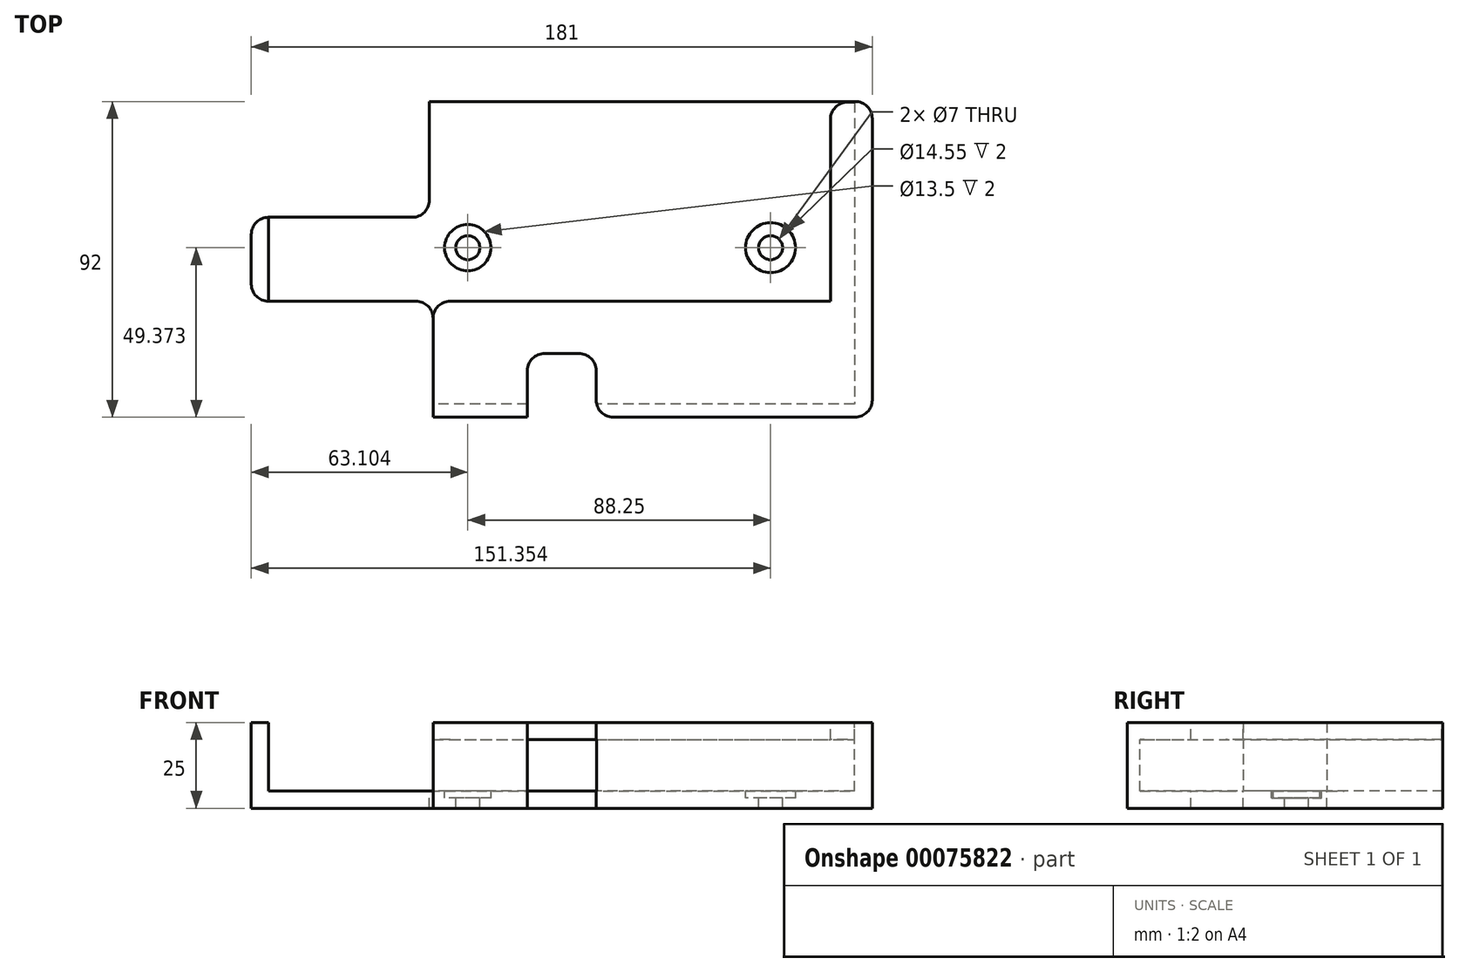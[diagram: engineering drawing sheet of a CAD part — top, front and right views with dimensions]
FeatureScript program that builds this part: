
annotation { "Feature Type Name" : "Feature", "Feature Type Description" : "" }
export const myFeature = defineFeature(function(context is Context, id is Id, definition is map)
    precondition{}
    {
        {
            var Q0;
            Q0=qCreatedBy(makeId("Top.planeOp"),FACE);
            var sketch = newSketch(context, id + "F0", { "sketchPlane" : qUnion([Q0])});
            skLineSegment(sketch, "E0.bottom", {"start": v(-90.5, 55.49) * mm, "end": v(90.5, 55.49) * mm});
            skLineSegment(sketch, "E0.top", {"start": v(-90.5, -36.51) * mm, "end": v(90.5, -36.51) * mm});
            skLineSegment(sketch, "E0.left", {"start": v(-90.5, 55.49) * mm, "end": v(-90.5, -36.51) * mm});
            skLineSegment(sketch, "E0.right", {"start": v(90.5, 55.49) * mm, "end": v(90.5, -36.51) * mm});
            skLineSegment(sketch, "E1.bottom", {"start": v(-25, 55.49) * mm, "end": v(25, 55.49) * mm});
            skSolve(sketch);
        }
        {
            var Q0;
            {var subQ5=sQuery(id+"F0.wireOp",EDGE,"E0.right");Q0=makeQuery(id+"F0.imprint","IMPRINT",FACE,{"disambiguationData":[TD([[makeQuery(id+"F0.imprint","IMPRINT",EDGE,{"derivedFrom":subQ5}),-1.0]])]});}
            var Q1;
            {var subQ7=sQuery(id+"F0.wireOp",EDGE,"E0.left");Q1=makeQuery(id+"F0.imprint","IMPRINT",FACE,{"disambiguationData":[TD([[makeQuery(id+"F0.imprint","IMPRINT",EDGE,{"derivedFrom":subQ7}),1.0]])]});}
            var Q2;
            {var subQ0=sQuery(id+"F0.wireOp",EDGE,"E1.right");Q2=makeQuery(id+"F0.imprint","IMPRINT",FACE,{"disambiguationData":[TD([[makeQuery(id+"F0.imprint","IMPRINT",EDGE,{"derivedFrom":subQ0}),1.0]])]});}
            var Q3;
            {var subQ0=sQuery(id+"F0.wireOp",EDGE,"E1.left");Q3=makeQuery(id+"F0.imprint","IMPRINT",FACE,{"disambiguationData":[TD([[makeQuery(id+"F0.imprint","IMPRINT",EDGE,{"derivedFrom":subQ0}),-1.0]])]});}
            extrude(context, id + "F1", {"entities" : qUnion([Q0, Q1, Q2, Q3]), "depth" : 25 * mm});
        }
        {
            var Q0;
            Q0=makeQuery(id+"F1.opExtrude","CAP_FACE",FACE,{"disambiguationData":[OSD([sQuery(id+"F0.wireOp",EDGE,"E0.bottom"),sQuery(id+"F0.wireOp",EDGE,"E0.top"),sQuery(id+"F0.wireOp",EDGE,"E0.left"),sQuery(id+"F0.wireOp",EDGE,"E0.right"),sQuery(id+"F0.wireOp",EDGE,"E1.top"),sQuery(id+"F0.wireOp",EDGE,"E1.left"),sQuery(id+"F0.wireOp",EDGE,"E1.right")])],"isStart":false});
            var sketch = newSketch(context, id + "F2", { "sketchPlane" : qUnion([Q0])});
            skLineSegment(sketch, "E2.bottom", {"start": v(-85, 55.49) * mm, "end": v(85, 55.49) * mm});
            skLineSegment(sketch, "E2.top", {"start": v(-85, -30.32) * mm, "end": v(85, -30.32) * mm});
            skLineSegment(sketch, "E2.left", {"start": v(-85, 55.49) * mm, "end": v(-85, -30.32) * mm});
            skLineSegment(sketch, "E2.right", {"start": v(85, 55.49) * mm, "end": v(85, -30.32) * mm});
            skLineSegment(sketch, "E3", {"start": v(0, 55.49) * mm, "end": v(0, 0) * mm});
            skPoint(sketch, "E3.startSnap0", {"position": v(0, 55.49) * mm});
            skLineSegment(sketch, "E4", {"start": v(0, 0) * mm, "end": v(0, -30.32) * mm});
            skLineSegment(sketch, "E5", {"start": v(-85, 0) * mm, "end": v(0, 0) * mm});
            skLineSegment(sketch, "E6", {"start": v(85, 0) * mm, "end": v(0, 0) * mm});
            skSolve(sketch);
        }
        {
            var Q0;
            Q0=makeQuery(id+"F2.imprint","IMPRINT",FACE,{"disambiguationData":[TD([[makeQuery(id+"F2.imprint","IMPRINT",EDGE,{"derivedFrom":makeQuery(id+"F1.opExtrude","CAP_EDGE",EDGE,{"disambiguationData":[OSD([sQuery(id+"F0.wireOp",EDGE,"E0.top")])],"isStart":false})}),1.0]])]});
            var sketch = newSketch(context, id + "F3", { "sketchPlane" : qUnion([Q0])});
            skPoint(sketch, "E7", {"position": v(0, -17.95) * mm});
            skLineSegment(sketch, "E8", {"start": v(0, -17.95) * mm, "end": v(10, -17.95) * mm});
            skLineSegment(sketch, "E9", {"start": v(10, -17.95) * mm, "end": v(10, -36.51) * mm});
            skLineSegment(sketch, "E10", {"start": v(0, -17.95) * mm, "end": v(-10, -17.95) * mm});
            skLineSegment(sketch, "E11", {"start": v(-10, -17.95) * mm, "end": v(-10, -36.51) * mm});
            skSolve(sketch);
        }
        {
            var Q0;
            {var subQ7=makeQuery(id+"F2.imprint","IMPRINT",EDGE,{"derivedFrom":makeQuery(id+"F1.opExtrude","CAP_EDGE",EDGE,{"disambiguationData":[OSD([sQuery(id+"F0.wireOp",EDGE,"E0.top")])],"isStart":false})});var subQ9=sQuery(id+"F3.wireOp",EDGE,"E9");var subQ11=makeQuery(id+"F3.imprint","INTERSECT",VERTEX,{"derivedFrom":[subQ7,subQ9]});Q0=makeQuery(id+"F3.imprint","IMPRINT",FACE,{"disambiguationData":[TD([[makeQuery(id+"F3.imprint","IMPRINT",EDGE,{"disambiguationData":[TD([[subQ11,1.0]])],"derivedFrom":subQ7}),1.0]])]});}
            var Q1;
            {var subQ2=sQuery(id+"F3.wireOp",EDGE,"E8");Q1=makeQuery(id+"F3.imprint","IMPRINT",FACE,{"disambiguationData":[TD([[makeQuery(id+"F3.imprint","IMPRINT",EDGE,{"derivedFrom":subQ2}),-1.0]])]});}
            extrude(context, id + "F4", {"entities" : qUnion([Q0, Q1]), "operationType" : NewBodyOperationType.REMOVE, "oppositeDirection" : true, "depth" : 25 * mm});
        }
        {
            var Q0;
            Q0=makeQuery(id+"F1.opExtrude","CAP_FACE",FACE,{"disambiguationData":[OSD([sQuery(id+"F0.wireOp",EDGE,"E0.bottom"),sQuery(id+"F0.wireOp",EDGE,"E0.top"),sQuery(id+"F0.wireOp",EDGE,"E0.left"),sQuery(id+"F0.wireOp",EDGE,"E0.right"),sQuery(id+"F0.wireOp",EDGE,"E1.top"),sQuery(id+"F0.wireOp",EDGE,"E1.left"),sQuery(id+"F0.wireOp",EDGE,"E1.right")])],"isStart":false});
            var sketch = newSketch(context, id + "F5", { "sketchPlane" : qUnion([Q0])});
            skLineSegment(sketch, "E12", {"start": v(83.31, 55.49) * mm, "end": v(83.31, -2.74) * mm});
            skLineSegment(sketch, "E13", {"start": v(83.31, -2.74) * mm, "end": v(-37.52, -2.74) * mm});
            skLineSegment(sketch, "E14", {"start": v(-37.52, -2.74) * mm, "end": v(-37.52, -36.51) * mm});
            skSolve(sketch);
        }
        {
            var Q0;
            {var subQ7=sQuery(id+"F5.wireOp",EDGE,"E12");Q0=makeQuery(id+"F5.imprint","IMPRINT",FACE,{"disambiguationData":[TD([[makeQuery(id+"F5.imprint","IMPRINT",EDGE,{"derivedFrom":subQ7}),-1.0]])]});}
            extrude(context, id + "F6", {"entities" : qUnion([Q0]), "operationType" : NewBodyOperationType.REMOVE, "oppositeDirection" : true, "depth" : 20 * mm});
        }
        {
            var Q0;
            Q0=makeQuery(id+"F6.boolean.opBoolean","COPY",FACE,{"derivedFrom":makeQuery(id+"F6.opExtrude","CAP_FACE",FACE,{"disambiguationData":[OSD([sQuery(id+"F0.wireOp",EDGE,"E0.bottom"),sQuery(id+"F0.wireOp",EDGE,"E0.top"),sQuery(id+"F0.wireOp",EDGE,"E0.left"),sQuery(id+"F0.wireOp",EDGE,"E1.top"),sQuery(id+"F0.wireOp",EDGE,"E1.left"),sQuery(id+"F0.wireOp",EDGE,"E1.right"),sQuery(id+"F5.wireOp",EDGE,"E12"),sQuery(id+"F5.wireOp",EDGE,"E13"),sQuery(id+"F5.wireOp",EDGE,"E14")])],"isStart":false})});
            var sketch = newSketch(context, id + "F7", { "sketchPlane" : qUnion([Q0])});
            skLineSegment(sketch, "E15.bottom", {"start": v(-37.52, -2.74) * mm, "end": v(-90.5, -2.74) * mm});
            skLineSegment(sketch, "E15.top", {"start": v(-37.52, -36.51) * mm, "end": v(-90.5, -36.51) * mm});
            skLineSegment(sketch, "E15.left", {"start": v(-37.52, -2.74) * mm, "end": v(-37.52, -36.51) * mm});
            skLineSegment(sketch, "E15.right", {"start": v(-90.5, -2.74) * mm, "end": v(-90.5, -36.51) * mm});
            skLineSegment(sketch, "E16.bottom", {"start": v(-90.5, 55.49) * mm, "end": v(-38.59, 55.49) * mm});
            skLineSegment(sketch, "E16.top", {"start": v(-90.5, 21.71) * mm, "end": v(-38.59, 21.71) * mm});
            skLineSegment(sketch, "E16.left", {"start": v(-90.5, 55.49) * mm, "end": v(-90.5, 21.71) * mm});
            skLineSegment(sketch, "E16.right", {"start": v(-38.59, 55.49) * mm, "end": v(-38.59, 21.71) * mm});
            skSolve(sketch);
        }
        {
            var Q0;
            Q0=makeQuery(id+"F7.imprint","IMPRINT",FACE,{"disambiguationData":[TD([[makeQuery(id+"F7.imprint","IMPRINT",EDGE,{"derivedFrom":sQuery(id+"F7.wireOp",EDGE,"E16.bottom")}),-1.0]])]});
            var Q1;
            Q1=makeQuery(id+"F7.imprint","IMPRINT",FACE,{"disambiguationData":[TD([[makeQuery(id+"F7.imprint","IMPRINT",EDGE,{"derivedFrom":sQuery(id+"F7.wireOp",EDGE,"E15.bottom")}),1.0]])]});
            extrude(context, id + "F8", {"entities" : qUnion([Q0, Q1]), "operationType" : NewBodyOperationType.REMOVE, "oppositeDirection" : true, "depth" : 25 * mm});
        }
        {
            var Q0;
            Q0=makeQuery(id+"F6.boolean.opBoolean","COPY",FACE,{"derivedFrom":makeQuery(id+"F6.opExtrude","CAP_FACE",FACE,{"disambiguationData":[OSD([sQuery(id+"F0.wireOp",EDGE,"E0.bottom"),sQuery(id+"F0.wireOp",EDGE,"E0.top"),sQuery(id+"F0.wireOp",EDGE,"E0.left"),sQuery(id+"F0.wireOp",EDGE,"E1.top"),sQuery(id+"F0.wireOp",EDGE,"E1.left"),sQuery(id+"F0.wireOp",EDGE,"E1.right"),sQuery(id+"F5.wireOp",EDGE,"E12"),sQuery(id+"F5.wireOp",EDGE,"E13"),sQuery(id+"F5.wireOp",EDGE,"E14")])],"isStart":false})});
            var sketch = newSketch(context, id + "F9", { "sketchPlane" : qUnion([Q0])});
            skLineSegment(sketch, "E17", {"start": v(-90.5, 21.71) * mm, "end": v(-85.5, 21.71) * mm});
            skLineSegment(sketch, "E18", {"start": v(-85.5, 21.71) * mm, "end": v(-85.5, -2.74) * mm});
            skSolve(sketch);
        }
        {
            var Q0;
            Q0=makeQuery(id+"F9.imprint","IMPRINT",FACE,{"disambiguationData":[TD([[makeQuery(id+"F9.imprint","IMPRINT",EDGE,{"derivedFrom":sQuery(id+"F9.wireOp",EDGE,"E17")}),-1.0]])]});
            extrude(context, id + "F10", {"entities" : qUnion([Q0]), "operationType" : NewBodyOperationType.ADD, "depth" : 20 * mm});
        }
        {
            var Q0;
            Q0=makeQuery(id+"F6.boolean.opBoolean","COPY",FACE,{"derivedFrom":makeQuery(id+"F6.opExtrude","SWEPT_FACE",FACE,{"disambiguationData":[OSD([sQuery(id+"F5.wireOp",EDGE,"E13")])]})});
            var sketch = newSketch(context, id + "F11", { "sketchPlane" : qUnion([Q0])});
            skLineSegment(sketch, "E19.bottom", {"start": v(37.52, 5) * mm, "end": v(-83.31, 5) * mm});
            skLineSegment(sketch, "E19.top", {"start": v(37.52, 20) * mm, "end": v(-83.31, 20) * mm});
            skLineSegment(sketch, "E19.left", {"start": v(37.52, 5) * mm, "end": v(37.52, 20) * mm});
            skLineSegment(sketch, "E19.right", {"start": v(-83.31, 5) * mm, "end": v(-83.31, 20) * mm});
            skLineSegment(sketch, "E20", {"start": v(37.52, 20) * mm, "end": v(37.52, 25) * mm});
            skSolve(sketch);
        }
        {
            var Q0;
            Q0=makeQuery(id+"F11.imprint","IMPRINT",FACE,{"disambiguationData":[TD([[makeQuery(id+"F11.imprint","IMPRINT",EDGE,{"derivedFrom":sQuery(id+"F11.wireOp",EDGE,"E19.bottom")}),1.0]])]});
            extrude(context, id + "F12", {"entities" : qUnion([Q0]), "operationType" : NewBodyOperationType.REMOVE, "oppositeDirection" : true, "depth" : 30 * mm});
        }
        {
            var Q0;
            Q0=makeQuery(id+"F12.boolean.opBoolean","MERGE",FACE,{"derivedFrom":[makeQuery(id+"F6.boolean.opBoolean","COPY",FACE,{"derivedFrom":makeQuery(id+"F6.opExtrude","CAP_FACE",FACE,{"disambiguationData":[OSD([sQuery(id+"F0.wireOp",EDGE,"E0.bottom"),sQuery(id+"F0.wireOp",EDGE,"E0.top"),sQuery(id+"F0.wireOp",EDGE,"E0.left"),sQuery(id+"F0.wireOp",EDGE,"E1.top"),sQuery(id+"F0.wireOp",EDGE,"E1.left"),sQuery(id+"F0.wireOp",EDGE,"E1.right"),sQuery(id+"F5.wireOp",EDGE,"E12"),sQuery(id+"F5.wireOp",EDGE,"E13"),sQuery(id+"F5.wireOp",EDGE,"E14")])],"isStart":false})}),makeQuery(id+"F12.opExtrude","SWEPT_FACE",FACE,{"disambiguationData":[OSD([sQuery(id+"F11.wireOp",EDGE,"E19.bottom")])]})]});
            var sketch = newSketch(context, id + "F13", { "sketchPlane" : qUnion([Q0])});
            skLineSegment(sketch, "E21", {"start": v(-85.5, 12.86) * mm, "end": v(-27.4, 12.86) * mm});
            skLineSegment(sketch, "E22", {"start": v(-27.4, 12.86) * mm, "end": v(60.85, 12.86) * mm});
            skLineSegment(sketch, "E23", {"start": v(60.85, 12.86) * mm, "end": v(83.31, 12.86) * mm});
            skCircle(sketch, "E24", {"center": v(-27.4, 12.86) * mm, "radius": 3.5 * mm});
            skCircle(sketch, "E25", {"center": v(60.85, 12.86) * mm, "radius": 3.5 * mm});
            skSolve(sketch);
        }
        {
            var Q0;
            {var subQ0=sQuery(id+"F13.wireOp",EDGE,"E23");var subQ1=sQuery(id+"F13.wireOp",EDGE,"E22");var subQ2=makeQuery(id+"F13.imprint","INTERSECT",VERTEX,{"derivedFrom":[subQ1,subQ0]});Q0=makeQuery(id+"F13.imprint","IMPRINT",FACE,{"disambiguationData":[TD([[makeQuery(id+"F13.imprint","IMPRINT",EDGE,{"disambiguationData":[TD([[subQ2,1.0]])],"derivedFrom":subQ1}),1.0]])]});}
            var Q1;
            {var subQ0=sQuery(id+"F13.wireOp",EDGE,"E23");var subQ1=sQuery(id+"F13.wireOp",EDGE,"E22");var subQ2=makeQuery(id+"F13.imprint","INTERSECT",VERTEX,{"derivedFrom":[subQ1,subQ0]});Q1=makeQuery(id+"F13.imprint","IMPRINT",FACE,{"disambiguationData":[TD([[makeQuery(id+"F13.imprint","IMPRINT",EDGE,{"disambiguationData":[TD([[subQ2,1.0]])],"derivedFrom":subQ1}),-1.0]])]});}
            var Q2;
            {var subQ0=sQuery(id+"F13.wireOp",EDGE,"E22");var subQ1=sQuery(id+"F13.wireOp",EDGE,"E21");var subQ2=makeQuery(id+"F13.imprint","INTERSECT",VERTEX,{"derivedFrom":[subQ1,subQ0]});Q2=makeQuery(id+"F13.imprint","IMPRINT",FACE,{"disambiguationData":[TD([[makeQuery(id+"F13.imprint","IMPRINT",EDGE,{"disambiguationData":[TD([[subQ2,1.0]])],"derivedFrom":subQ1}),1.0]])]});}
            var Q3;
            {var subQ0=sQuery(id+"F13.wireOp",EDGE,"E22");var subQ1=sQuery(id+"F13.wireOp",EDGE,"E21");var subQ2=makeQuery(id+"F13.imprint","INTERSECT",VERTEX,{"derivedFrom":[subQ1,subQ0]});Q3=makeQuery(id+"F13.imprint","IMPRINT",FACE,{"disambiguationData":[TD([[makeQuery(id+"F13.imprint","IMPRINT",EDGE,{"disambiguationData":[TD([[subQ2,1.0]])],"derivedFrom":subQ1}),-1.0]])]});}
            extrude(context, id + "F14", {"entities" : qUnion([Q0, Q1, Q2, Q3]), "operationType" : NewBodyOperationType.REMOVE, "oppositeDirection" : true, "depth" : 6 * mm});
        }
        {
            var Q0;
            Q0=makeQuery(id+"F12.boolean.opBoolean","MERGE",FACE,{"derivedFrom":[makeQuery(id+"F6.boolean.opBoolean","COPY",FACE,{"derivedFrom":makeQuery(id+"F6.opExtrude","CAP_FACE",FACE,{"disambiguationData":[OSD([sQuery(id+"F0.wireOp",EDGE,"E0.bottom"),sQuery(id+"F0.wireOp",EDGE,"E0.top"),sQuery(id+"F0.wireOp",EDGE,"E0.left"),sQuery(id+"F0.wireOp",EDGE,"E1.top"),sQuery(id+"F0.wireOp",EDGE,"E1.left"),sQuery(id+"F0.wireOp",EDGE,"E1.right"),sQuery(id+"F5.wireOp",EDGE,"E12"),sQuery(id+"F5.wireOp",EDGE,"E13"),sQuery(id+"F5.wireOp",EDGE,"E14")])],"isStart":false})}),makeQuery(id+"F12.opExtrude","SWEPT_FACE",FACE,{"disambiguationData":[OSD([sQuery(id+"F11.wireOp",EDGE,"E19.bottom")])]})]});
            var sketch = newSketch(context, id + "F15", { "sketchPlane" : qUnion([Q0])});
            skCircle(sketch, "E26", {"center": v(-27.4, 12.86) * mm, "radius": 6.75 * mm});
            skCircle(sketch, "E27", {"center": v(60.85, 12.86) * mm, "radius": 7.28 * mm});
            skSolve(sketch);
        }
        {
            var Q0;
            Q0=makeQuery(id+"F15.imprint","IMPRINT",FACE,{"disambiguationData":[TD([[makeQuery(id+"F15.imprint","IMPRINT",EDGE,{"derivedFrom":sQuery(id+"F15.wireOp",EDGE,"E27")}),1.0]])]});
            var Q1;
            Q1=makeQuery(id+"F15.imprint","IMPRINT",FACE,{"disambiguationData":[TD([[makeQuery(id+"F15.imprint","IMPRINT",EDGE,{"derivedFrom":sQuery(id+"F15.wireOp",EDGE,"E26")}),1.0]])]});
            extrude(context, id + "F16", {"entities" : qUnion([Q0, Q1]), "operationType" : NewBodyOperationType.REMOVE, "oppositeDirection" : true, "depth" : 2 * mm});
        }
        {
            var Q0;
            Q0=makeQuery(id+"F6.boolean.opBoolean","COPY",FACE,{"derivedFrom":makeQuery(id+"F6.opExtrude","SWEPT_FACE",FACE,{"disambiguationData":[OSD([sQuery(id+"F5.wireOp",EDGE,"E13")])]})});
            var sketch = newSketch(context, id + "F17", { "sketchPlane" : qUnion([Q0])});
            skLineSegment(sketch, "E28", {"start": v(-83.31, 20) * mm, "end": v(-78.31, 20) * mm});
            skLineSegment(sketch, "E29", {"start": v(-78.31, 20) * mm, "end": v(-78.31, 25) * mm});
            skSolve(sketch);
        }
        {
            var Q0;
            Q0=makeQuery(id+"F17.imprint","IMPRINT",FACE,{"disambiguationData":[TD([[makeQuery(id+"F17.imprint","IMPRINT",EDGE,{"derivedFrom":sQuery(id+"F17.wireOp",EDGE,"E28")}),-1.0]])]});
            extrude(context, id + "F18", {"entities" : qUnion([Q0]), "operationType" : NewBodyOperationType.ADD, "depth" : 58 * mm});
        }
        {
            var Q0;
            Q0=makeQuery(id+"F12.boolean.opBoolean","MERGE",FACE,{"derivedFrom":[makeQuery(id+"F6.boolean.opBoolean","COPY",FACE,{"derivedFrom":makeQuery(id+"F6.opExtrude","SWEPT_FACE",FACE,{"disambiguationData":[OSD([sQuery(id+"F5.wireOp",EDGE,"E12")])]})}),makeQuery(id+"F12.opExtrude","SWEPT_FACE",FACE,{"disambiguationData":[OSD([sQuery(id+"F11.wireOp",EDGE,"E19.right")])]})]});
            extrude(context, id + "F19", {"entities" : qUnion([Q0]), "operationType" : NewBodyOperationType.REMOVE, "oppositeDirection" : true, "depth" : 2 * mm});
        }
        {
            var Q0;
            Q0=makeQuery(id+"F4.boolean.opBoolean","COPY",EDGE,{"derivedFrom":makeQuery(id+"F4.opExtrude","SWEPT_EDGE",EDGE,{"disambiguationData":[OSD([sQuery(id+"F0.wireOp",EDGE,"E0.top"),sQuery(id+"F3.wireOp",EDGE,"E11")])]})});
            var Q1;
            {var subQ0=sQuery(id+"F3.wireOp",EDGE,"E10");var subQ1=sQuery(id+"F3.wireOp",EDGE,"E11");Q1=makeQuery(id+"F12.boolean.opBoolean","SPLIT",EDGE,{"disambiguationData":[TD([makeQuery(id+"F12.opExtrude","SWEPT_FACE",FACE,{"disambiguationData":[OSD([sQuery(id+"F11.wireOp",EDGE,"E19.top")])]})])],"derivedFrom":makeQuery(id+"F4.boolean.opBoolean","COPY",EDGE,{"derivedFrom":makeQuery(id+"F4.opExtrude","SWEPT_EDGE",EDGE,{"disambiguationData":[OSD([subQ0,subQ1])]})})});}
            var Q2;
            {var subQ4=sQuery(id+"F3.wireOp",EDGE,"E11");var subQ5=sQuery(id+"F3.wireOp",EDGE,"E10");Q2=makeQuery(id+"F12.boolean.opBoolean","SPLIT",EDGE,{"disambiguationData":[TD([makeQuery(id+"F12.opExtrude","SWEPT_FACE",FACE,{"disambiguationData":[OSD([sQuery(id+"F11.wireOp",EDGE,"E19.bottom")])]})])],"derivedFrom":makeQuery(id+"F4.boolean.opBoolean","COPY",EDGE,{"derivedFrom":makeQuery(id+"F4.opExtrude","SWEPT_EDGE",EDGE,{"disambiguationData":[OSD([subQ5,subQ4])]})})});}
            var Q3;
            {var subQ0=sQuery(id+"F3.wireOp",EDGE,"E8");var subQ1=sQuery(id+"F3.wireOp",EDGE,"E9");Q3=makeQuery(id+"F12.boolean.opBoolean","SPLIT",EDGE,{"disambiguationData":[TD([makeQuery(id+"F12.opExtrude","SWEPT_FACE",FACE,{"disambiguationData":[OSD([sQuery(id+"F11.wireOp",EDGE,"E19.top")])]})])],"derivedFrom":makeQuery(id+"F4.boolean.opBoolean","COPY",EDGE,{"derivedFrom":makeQuery(id+"F4.opExtrude","SWEPT_EDGE",EDGE,{"disambiguationData":[OSD([subQ0,subQ1])]})})});}
            var Q4;
            {var subQ4=sQuery(id+"F3.wireOp",EDGE,"E9");var subQ5=sQuery(id+"F3.wireOp",EDGE,"E8");Q4=makeQuery(id+"F12.boolean.opBoolean","SPLIT",EDGE,{"disambiguationData":[TD([makeQuery(id+"F12.opExtrude","SWEPT_FACE",FACE,{"disambiguationData":[OSD([sQuery(id+"F11.wireOp",EDGE,"E19.bottom")])]})])],"derivedFrom":makeQuery(id+"F4.boolean.opBoolean","COPY",EDGE,{"derivedFrom":makeQuery(id+"F4.opExtrude","SWEPT_EDGE",EDGE,{"disambiguationData":[OSD([subQ5,subQ4])]})})});}
            var Q5;
            Q5=makeQuery(id+"F4.boolean.opBoolean","COPY",EDGE,{"derivedFrom":makeQuery(id+"F4.opExtrude","SWEPT_EDGE",EDGE,{"disambiguationData":[OSD([sQuery(id+"F0.wireOp",EDGE,"E0.top"),sQuery(id+"F3.wireOp",EDGE,"E9")])]})});
            var Q6;
            Q6=makeQuery(id+"F8.boolean.opBoolean","MERGE",EDGE,{"derivedFrom":[makeQuery(id+"F6.boolean.opBoolean","COPY",EDGE,{"derivedFrom":makeQuery(id+"F6.opExtrude","SWEPT_EDGE",EDGE,{"disambiguationData":[OSD([sQuery(id+"F0.wireOp",EDGE,"E0.top"),sQuery(id+"F5.wireOp",EDGE,"E14")])]})}),makeQuery(id+"F8.opExtrude","SWEPT_EDGE",EDGE,{"disambiguationData":[OSD([sQuery(id+"F7.wireOp",EDGE,"E15.top"),sQuery(id+"F7.wireOp",EDGE,"E15.left")])]})]});
            var Q7;
            Q7=makeQuery(id+"F8.boolean.opBoolean","COPY",EDGE,{"derivedFrom":makeQuery(id+"F8.opExtrude","SWEPT_EDGE",EDGE,{"disambiguationData":[OSD([sQuery(id+"F0.wireOp",EDGE,"E0.bottom"),sQuery(id+"F0.wireOp",EDGE,"E1.bottom"),sQuery(id+"F7.wireOp",EDGE,"E16.bottom"),sQuery(id+"F7.wireOp",EDGE,"E16.right")])]})});
            var Q8;
            Q8=makeQuery(id+"F1.opExtrude","SWEPT_EDGE",EDGE,{"disambiguationData":[OSD([sQuery(id+"F0.wireOp",EDGE,"E0.bottom"),sQuery(id+"F0.wireOp",EDGE,"E0.right")])]});
            var Q9;
            Q9=makeQuery(id+"F1.opExtrude","SWEPT_EDGE",EDGE,{"disambiguationData":[OSD([sQuery(id+"F0.wireOp",EDGE,"E0.top"),sQuery(id+"F0.wireOp",EDGE,"E0.right")])]});
            var Q10;
            Q10=makeQuery(id+"F8.boolean.opBoolean","COPY",EDGE,{"derivedFrom":makeQuery(id+"F8.opExtrude","SWEPT_EDGE",EDGE,{"disambiguationData":[OSD([sQuery(id+"F5.wireOp",EDGE,"E13"),sQuery(id+"F7.wireOp",EDGE,"E15.bottom"),sQuery(id+"F7.wireOp",EDGE,"E15.left")])]})});
            var Q11;
            Q11=makeQuery(id+"F8.boolean.opBoolean","COPY",EDGE,{"derivedFrom":makeQuery(id+"F8.opExtrude","SWEPT_EDGE",EDGE,{"disambiguationData":[OSD([sQuery(id+"F7.wireOp",EDGE,"E16.top"),sQuery(id+"F7.wireOp",EDGE,"E16.right")])]})});
            var Q12;
            {var subQ0=sQuery(id+"F0.wireOp",EDGE,"E0.left");Q12=makeQuery(id+"F10.boolean.opBoolean","MERGE",EDGE,{"derivedFrom":[makeQuery(id+"F8.boolean.opBoolean","COPY",EDGE,{"derivedFrom":makeQuery(id+"F8.opExtrude","SWEPT_EDGE",EDGE,{"disambiguationData":[OSD([subQ0,sQuery(id+"F7.wireOp",EDGE,"E16.top"),sQuery(id+"F7.wireOp",EDGE,"E16.left")])]})}),makeQuery(id+"F10.opExtrude","SWEPT_EDGE",EDGE,{"disambiguationData":[OSD([subQ0,sQuery(id+"F9.wireOp",EDGE,"E17")])]})]});}
            var Q13;
            {var subQ0=sQuery(id+"F7.wireOp",EDGE,"E15.bottom");var subQ1=sQuery(id+"F0.wireOp",EDGE,"E0.left");Q13=makeQuery(id+"F10.boolean.opBoolean","MERGE",EDGE,{"derivedFrom":[makeQuery(id+"F8.boolean.opBoolean","COPY",EDGE,{"derivedFrom":makeQuery(id+"F8.opExtrude","SWEPT_EDGE",EDGE,{"disambiguationData":[OSD([subQ1,subQ0,sQuery(id+"F7.wireOp",EDGE,"E15.right")])]})}),makeQuery(id+"F10.opExtrude","SWEPT_EDGE",EDGE,{"disambiguationData":[OSD([subQ1,subQ0])]})]});}
            var Q14;
            Q14=makeQuery(id+"F18.opExtrude","CAP_EDGE",EDGE,{"disambiguationData":[OSD([sQuery(id+"F17.wireOp",EDGE,"E29")])],"isStart":true});
            var Q15;
            Q15=makeQuery(id+"F18.opExtrude","CAP_EDGE",EDGE,{"disambiguationData":[OSD([sQuery(id+"F17.wireOp",EDGE,"E29")])],"isStart":false});
            var Q16;
            Q16=makeQuery(id+"F6.boolean.opBoolean","COPY",EDGE,{"derivedFrom":makeQuery(id+"F6.opExtrude","SWEPT_EDGE",EDGE,{"disambiguationData":[OSD([sQuery(id+"F5.wireOp",EDGE,"E13"),sQuery(id+"F5.wireOp",EDGE,"E14")])]})});
            fillet(context, id + "F20", {"entities" : qUnion([Q0, Q1, Q2, Q3, Q4, Q5, Q6, Q7, Q8, Q9, Q10, Q11, Q12, Q13, Q14, Q15, Q16]), "radius" : 5 * mm, "tangentPropagation" : true, "allowEdgeOverflow" : false});
        }
    });
